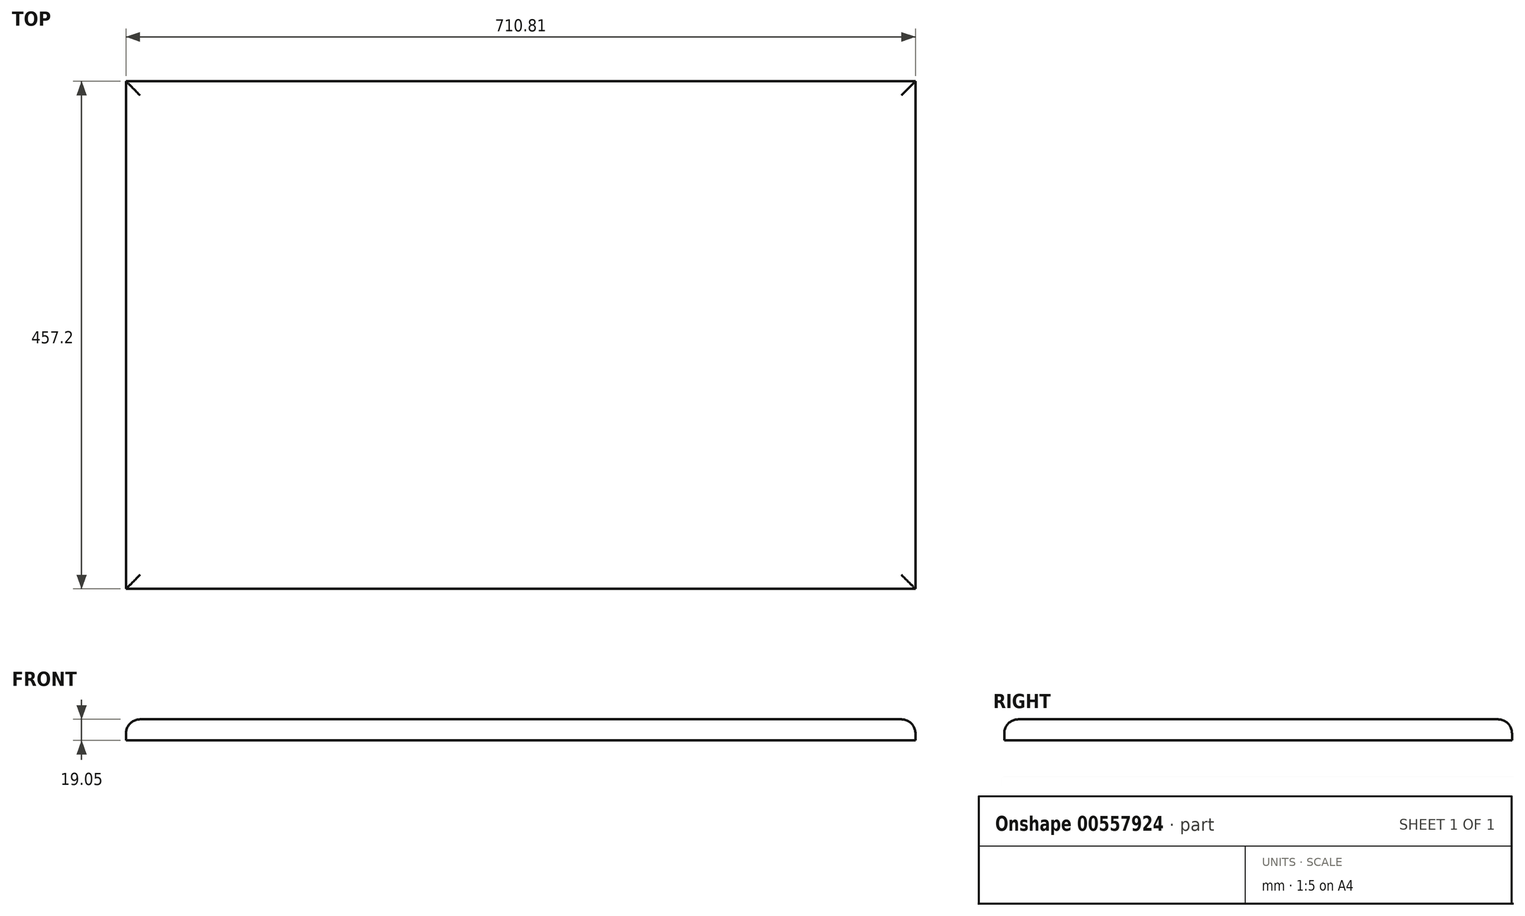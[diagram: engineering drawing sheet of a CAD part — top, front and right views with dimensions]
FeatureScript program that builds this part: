
annotation { "Feature Type Name" : "Feature", "Feature Type Description" : "" }
export const myFeature = defineFeature(function(context is Context, id is Id, definition is map)
    precondition{}
    {
        {
            var Q0;
            Q0=qCreatedBy(makeId("Top.planeOp"),FACE);
            var sketch = newSketch(context, id + "F0", { "sketchPlane" : qUnion([Q0])});
            skLineSegment(sketch, "E0.bottom", {"start": v(0, 0) * mm, "end": v(-710.8, 0) * mm});
            skLineSegment(sketch, "E0.top", {"start": v(0, 457.2) * mm, "end": v(-710.8, 457.2) * mm});
            skLineSegment(sketch, "E0.left", {"start": v(0, 0) * mm, "end": v(0, 457.2) * mm});
            skLineSegment(sketch, "E0.right", {"start": v(-710.8, 0) * mm, "end": v(-710.8, 457.2) * mm});
            skSolve(sketch);
        }
        {
            var Q0;
            Q0 = qSketchRegion(id + "F0", true);
            var Q1;
            Q1=makeQuery(id+"F0.imprint","IMPRINT",FACE,{"disambiguationData":[TD([[makeQuery(id+"F0.imprint","IMPRINT",EDGE,{"derivedFrom":sQuery(id+"F0.wireOp",EDGE,"E0.bottom")}),-1.0]])]});
            extrude(context, id + "F1", {"entities" : qUnion([Q0, Q1]), "depth" : 19.05 * mm, "offsetDistance" : 25.4 * mm});
        }
        {
            var Q0;
            Q0=makeQuery(id+"F1.opExtrude","CAP_EDGE",EDGE,{"disambiguationData":[OSD([sQuery(id+"F0.wireOp",EDGE,"E0.right")])],"isStart":false});
            var Q1;
            Q1=makeQuery(id+"F1.opExtrude","CAP_EDGE",EDGE,{"disambiguationData":[OSD([sQuery(id+"F0.wireOp",EDGE,"E0.top")])],"isStart":false});
            var Q2;
            Q2=makeQuery(id+"F1.opExtrude","CAP_EDGE",EDGE,{"disambiguationData":[OSD([sQuery(id+"F0.wireOp",EDGE,"E0.left")])],"isStart":false});
            var Q3;
            Q3=makeQuery(id+"F1.opExtrude","CAP_EDGE",EDGE,{"disambiguationData":[OSD([sQuery(id+"F0.wireOp",EDGE,"E0.bottom")])],"isStart":false});
            fillet(context, id + "F2", {"entities" : qUnion([Q0, Q1, Q2, Q3]), "radius" : 12.7 * mm, "tangentPropagation" : true, "allowEdgeOverflow" : false});
        }
    });
